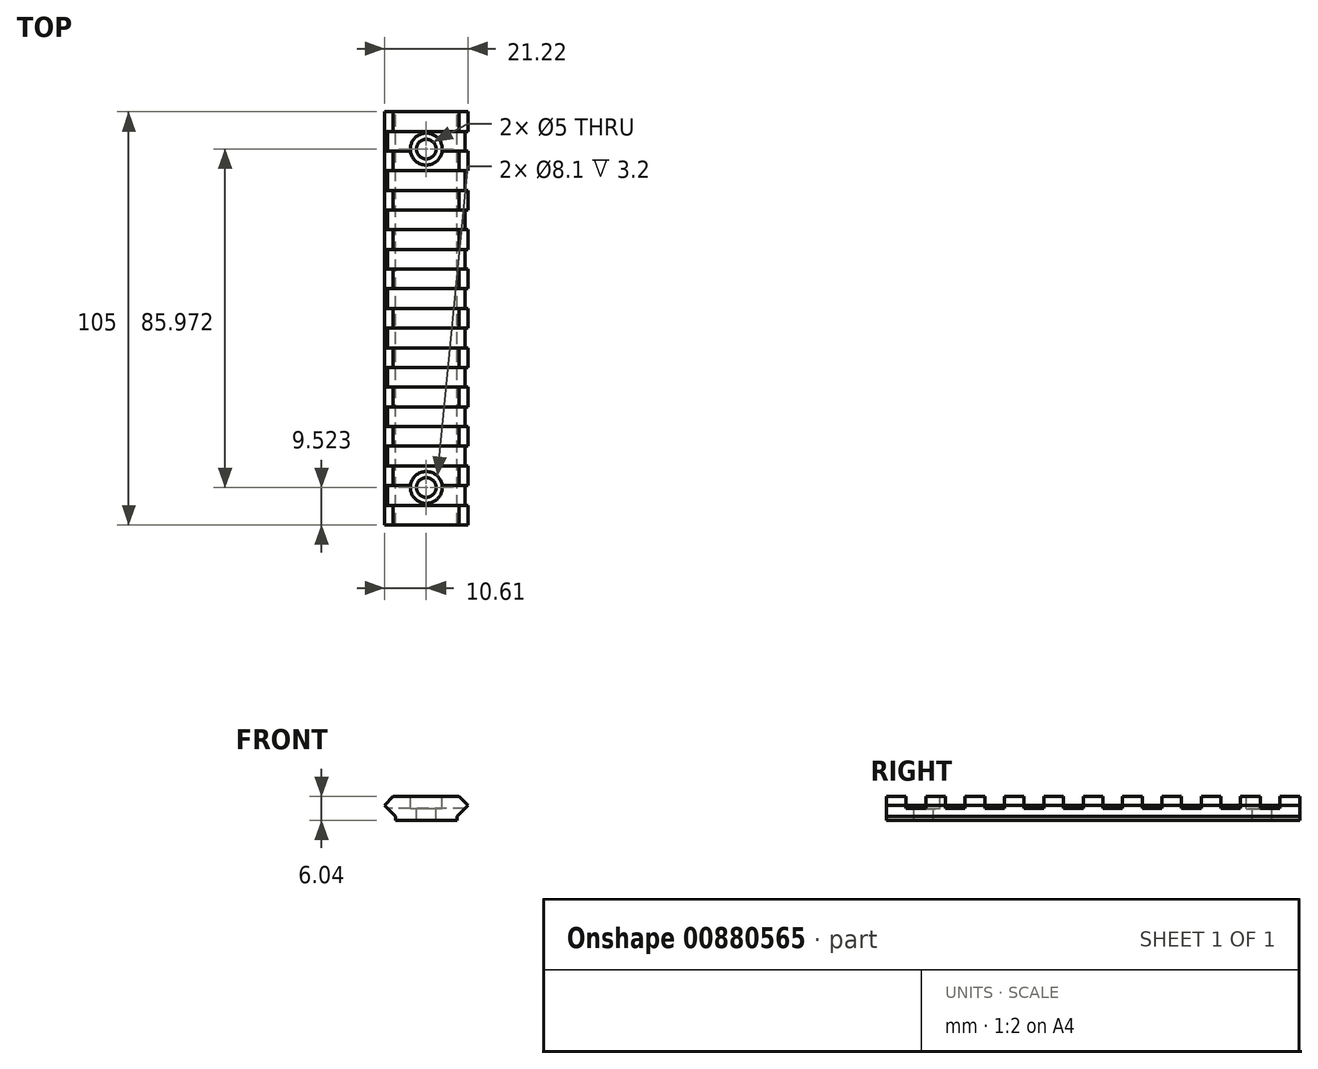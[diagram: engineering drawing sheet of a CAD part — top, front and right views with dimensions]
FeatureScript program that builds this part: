
annotation { "Feature Type Name" : "Feature", "Feature Type Description" : "" }
export const myFeature = defineFeature(function(context is Context, id is Id, definition is map)
    precondition{}
    {
        {
            var Q0;
            Q0=qCreatedBy(makeId("Front.planeOp"),FACE);
            var sketch = newSketch(context, id + "F0", { "sketchPlane" : qUnion([Q0])});
            skLineSegment(sketch, "E0", {"start": v(-7.8, -3.01) * mm, "end": v(7.81, -3.01) * mm});
            skLineSegment(sketch, "E1", {"start": v(7.81, -3.01) * mm, "end": v(7.81, -1.98) * mm});
            skLineSegment(sketch, "E2", {"start": v(7.81, -1.98) * mm, "end": v(10.6, 0.79) * mm});
            skLineSegment(sketch, "E3", {"start": v(10.6, 0.79) * mm, "end": v(8.39, 3.03) * mm});
            skLineSegment(sketch, "E4", {"start": v(8.39, 3.03) * mm, "end": v(-8.4, 3.03) * mm});
            skLineSegment(sketch, "E5", {"start": v(-8.4, 3.03) * mm, "end": v(-10.6, 0.79) * mm});
            skLineSegment(sketch, "E6", {"start": v(-10.6, 0.79) * mm, "end": v(-7.8, -1.98) * mm});
            skLineSegment(sketch, "E7", {"start": v(-7.8, -1.98) * mm, "end": v(-7.8, -3.01) * mm});
            skSolve(sketch);
        }
        {
            var Q0;
            Q0=qSketchRegion(id+"F0",true);
            extrude(context, id + "F1", {"entities" : qUnion([Q0]), "endBound" : BoundingType.SYMMETRIC, "depth" : 105 * mm, "offsetDistance" : 25 * mm});
        }
        {
            var Q0;
            Q0=qCreatedBy(makeId("Top.planeOp"),FACE);
            var sketch = newSketch(context, id + "F2", { "sketchPlane" : qUnion([Q0])});
            skLineSegment(sketch, "E8.bottom", {"start": v(10.61, -7.5) * mm, "end": v(-10.6, -7.5) * mm});
            skLineSegment(sketch, "E8.top", {"start": v(10.61, -2.5) * mm, "end": v(-10.6, -2.5) * mm});
            skLineSegment(sketch, "E8.left", {"start": v(10.61, -7.5) * mm, "end": v(10.61, -2.5) * mm});
            skLineSegment(sketch, "E8.right", {"start": v(-10.6, -7.5) * mm, "end": v(-10.6, -2.5) * mm});
            skLineSegment(sketch, "E9.0.1.0", {"start": v(10.61, -17.5) * mm, "end": v(-10.6, -17.5) * mm});
            skLineSegment(sketch, "E9.0.1.1", {"start": v(10.61, -12.5) * mm, "end": v(-10.6, -12.5) * mm});
            skLineSegment(sketch, "E9.0.1.2", {"start": v(10.61, -17.5) * mm, "end": v(10.61, -12.5) * mm});
            skLineSegment(sketch, "E9.0.1.3", {"start": v(-10.6, -17.5) * mm, "end": v(-10.6, -12.5) * mm});
            skLineSegment(sketch, "E9.0.2.0", {"start": v(10.61, -27.5) * mm, "end": v(-10.6, -27.5) * mm});
            skLineSegment(sketch, "E9.0.2.1", {"start": v(10.61, -22.5) * mm, "end": v(-10.6, -22.5) * mm});
            skLineSegment(sketch, "E9.0.2.2", {"start": v(10.61, -27.5) * mm, "end": v(10.61, -22.5) * mm});
            skLineSegment(sketch, "E9.0.2.3", {"start": v(-10.6, -27.5) * mm, "end": v(-10.6, -22.5) * mm});
            skLineSegment(sketch, "E9.0.3.0", {"start": v(10.61, -37.5) * mm, "end": v(-10.6, -37.5) * mm});
            skLineSegment(sketch, "E9.0.3.1", {"start": v(10.61, -32.5) * mm, "end": v(-10.6, -32.5) * mm});
            skLineSegment(sketch, "E9.0.3.2", {"start": v(10.61, -37.5) * mm, "end": v(10.61, -32.5) * mm});
            skLineSegment(sketch, "E9.0.3.3", {"start": v(-10.6, -37.5) * mm, "end": v(-10.6, -32.5) * mm});
            skLineSegment(sketch, "E9.0.4.0", {"start": v(10.61, -47.5) * mm, "end": v(-10.6, -47.5) * mm});
            skLineSegment(sketch, "E9.0.4.1", {"start": v(10.61, -42.5) * mm, "end": v(-10.6, -42.5) * mm});
            skLineSegment(sketch, "E9.0.4.2", {"start": v(10.61, -47.5) * mm, "end": v(10.61, -42.5) * mm});
            skLineSegment(sketch, "E9.0.4.3", {"start": v(-10.6, -47.5) * mm, "end": v(-10.6, -42.5) * mm});
            skLineSegment(sketch, "E9.direction1", {"start": v(-10.6, -7.5) * mm, "end": v(14.4, -7.5) * mm, "construction": true});
            skLineSegment(sketch, "E9.direction2", {"start": v(-10.6, -7.5) * mm, "end": v(-10.6, -17.5) * mm, "construction": true});
            skLineSegment(sketch, "E10.0.1.0", {"start": v(10.61, 7.5) * mm, "end": v(-10.6, 7.5) * mm});
            skLineSegment(sketch, "E10.0.1.1", {"start": v(10.61, 2.5) * mm, "end": v(10.61, 7.5) * mm});
            skLineSegment(sketch, "E10.0.1.2", {"start": v(-10.6, 2.5) * mm, "end": v(-10.6, 7.5) * mm});
            skLineSegment(sketch, "E10.0.1.3", {"start": v(10.61, 2.5) * mm, "end": v(-10.6, 2.5) * mm});
            skLineSegment(sketch, "E10.0.2.0", {"start": v(10.61, 17.5) * mm, "end": v(-10.6, 17.5) * mm});
            skLineSegment(sketch, "E10.0.2.1", {"start": v(10.61, 12.5) * mm, "end": v(10.61, 17.5) * mm});
            skLineSegment(sketch, "E10.0.2.2", {"start": v(-10.6, 12.5) * mm, "end": v(-10.6, 17.5) * mm});
            skLineSegment(sketch, "E10.0.2.3", {"start": v(10.61, 12.5) * mm, "end": v(-10.6, 12.5) * mm});
            skLineSegment(sketch, "E10.0.3.0", {"start": v(10.61, 27.5) * mm, "end": v(-10.6, 27.5) * mm});
            skLineSegment(sketch, "E10.0.3.1", {"start": v(10.61, 22.5) * mm, "end": v(10.61, 27.5) * mm});
            skLineSegment(sketch, "E10.0.3.2", {"start": v(-10.6, 22.5) * mm, "end": v(-10.6, 27.5) * mm});
            skLineSegment(sketch, "E10.0.3.3", {"start": v(10.61, 22.5) * mm, "end": v(-10.6, 22.5) * mm});
            skLineSegment(sketch, "E10.0.4.0", {"start": v(10.61, 37.5) * mm, "end": v(-10.6, 37.5) * mm});
            skLineSegment(sketch, "E10.0.4.1", {"start": v(10.61, 32.5) * mm, "end": v(10.61, 37.5) * mm});
            skLineSegment(sketch, "E10.0.4.2", {"start": v(-10.6, 32.5) * mm, "end": v(-10.6, 37.5) * mm});
            skLineSegment(sketch, "E10.0.4.3", {"start": v(10.61, 32.5) * mm, "end": v(-10.6, 32.5) * mm});
            skLineSegment(sketch, "E10.0.5.0", {"start": v(10.61, 47.5) * mm, "end": v(-10.6, 47.5) * mm});
            skLineSegment(sketch, "E10.0.5.1", {"start": v(10.61, 42.5) * mm, "end": v(10.61, 47.5) * mm});
            skLineSegment(sketch, "E10.0.5.2", {"start": v(-10.6, 42.5) * mm, "end": v(-10.6, 47.5) * mm});
            skLineSegment(sketch, "E10.0.5.3", {"start": v(10.61, 42.5) * mm, "end": v(-10.6, 42.5) * mm});
            skLineSegment(sketch, "E10.direction1", {"start": v(-10.6, -2.5) * mm, "end": v(14.4, -2.5) * mm, "construction": true});
            skLineSegment(sketch, "E10.direction2", {"start": v(-10.6, -2.5) * mm, "end": v(-10.6, 7.5) * mm, "construction": true});
            skSolve(sketch);
        }
        {
            var Q0;
            Q0=qSketchRegion(id+"F2",true);
            extrude(context, id + "F3", {"entities" : qUnion([Q0]), "operationType" : NewBodyOperationType.REMOVE, "depth" : 5 * mm, "offsetDistance" : 25 * mm});
        }
        {
            var Q0;
            Q0=makeQuery(id+"F3.boolean.opBoolean","SPLIT",FACE,{"disambiguationData":[TD([makeQuery(id+"F3.opExtrude","SWEPT_FACE",FACE,{"disambiguationData":[OSD([sQuery(id+"F2.wireOp",EDGE,"E10.0.4.0")])]})])],"derivedFrom":makeQuery(id+"F1.opExtrude","SWEPT_FACE",FACE,{"disambiguationData":[OSD([sQuery(id+"F0.wireOp",EDGE,"E4")])]})});
            var sketch = newSketch(context, id + "F4", { "sketchPlane" : qUnion([Q0])});
            skPoint(sketch, "E11", {"position": v(0, 43) * mm});
            skPoint(sketch, "E12", {"position": v(0, -42.98) * mm});
            skSolve(sketch);
        }
        {
            var Q0;
            Q0=sQuery(id+"F4.wireOp",VERTEX,"E11");
            var Q1;
            Q1=makeQuery(id+"F1.opExtrude","SWEPT_BODY",BODY,{"disambiguationData":[OSD([sQuery(id+"F0.wireOp",EDGE,"E0"),sQuery(id+"F0.wireOp",EDGE,"E1"),sQuery(id+"F0.wireOp",EDGE,"E2"),sQuery(id+"F0.wireOp",EDGE,"E3"),sQuery(id+"F0.wireOp",EDGE,"E4"),sQuery(id+"F0.wireOp",EDGE,"E5"),sQuery(id+"F0.wireOp",EDGE,"E6"),sQuery(id+"F0.wireOp",EDGE,"E7")])]});
            hole(context, id + "F5", {"style" : HoleStyle.C_BORE, "endStyle" : HoleEndStyle.BLIND, "holeDiameter" : 5 * mm, "cBoreDiameter" : 8.1 * mm, "cBoreDepth" : 3.2 * mm, "majorDiameter" : 5 * mm, "holeDepth" : 6.1 * mm, "isTappedThrough" : true, "tappedDepth" : 12 * mm, "tapClearance" : 3, "startFromSketch" : true, "locations" : qUnion([Q0]), "scope" : qUnion([Q1])});
        }
        {
            var Q0;
            Q0=sQuery(id+"F4.wireOp",VERTEX,"E12");
            var Q1;
            Q1=makeQuery(id+"F1.opExtrude","SWEPT_BODY",BODY,{"disambiguationData":[OSD([sQuery(id+"F0.wireOp",EDGE,"E0"),sQuery(id+"F0.wireOp",EDGE,"E1"),sQuery(id+"F0.wireOp",EDGE,"E2"),sQuery(id+"F0.wireOp",EDGE,"E3"),sQuery(id+"F0.wireOp",EDGE,"E4"),sQuery(id+"F0.wireOp",EDGE,"E5"),sQuery(id+"F0.wireOp",EDGE,"E6"),sQuery(id+"F0.wireOp",EDGE,"E7")])]});
            hole(context, id + "F6", {"style" : HoleStyle.C_BORE, "endStyle" : HoleEndStyle.BLIND, "holeDiameter" : 5 * mm, "cBoreDiameter" : 8.1 * mm, "cBoreDepth" : 3.2 * mm, "majorDiameter" : 5 * mm, "holeDepth" : 6.1 * mm, "isTappedThrough" : true, "tappedDepth" : 12 * mm, "tapClearance" : 3, "startFromSketch" : true, "locations" : qUnion([Q0]), "scope" : qUnion([Q1])});
        }
    });
